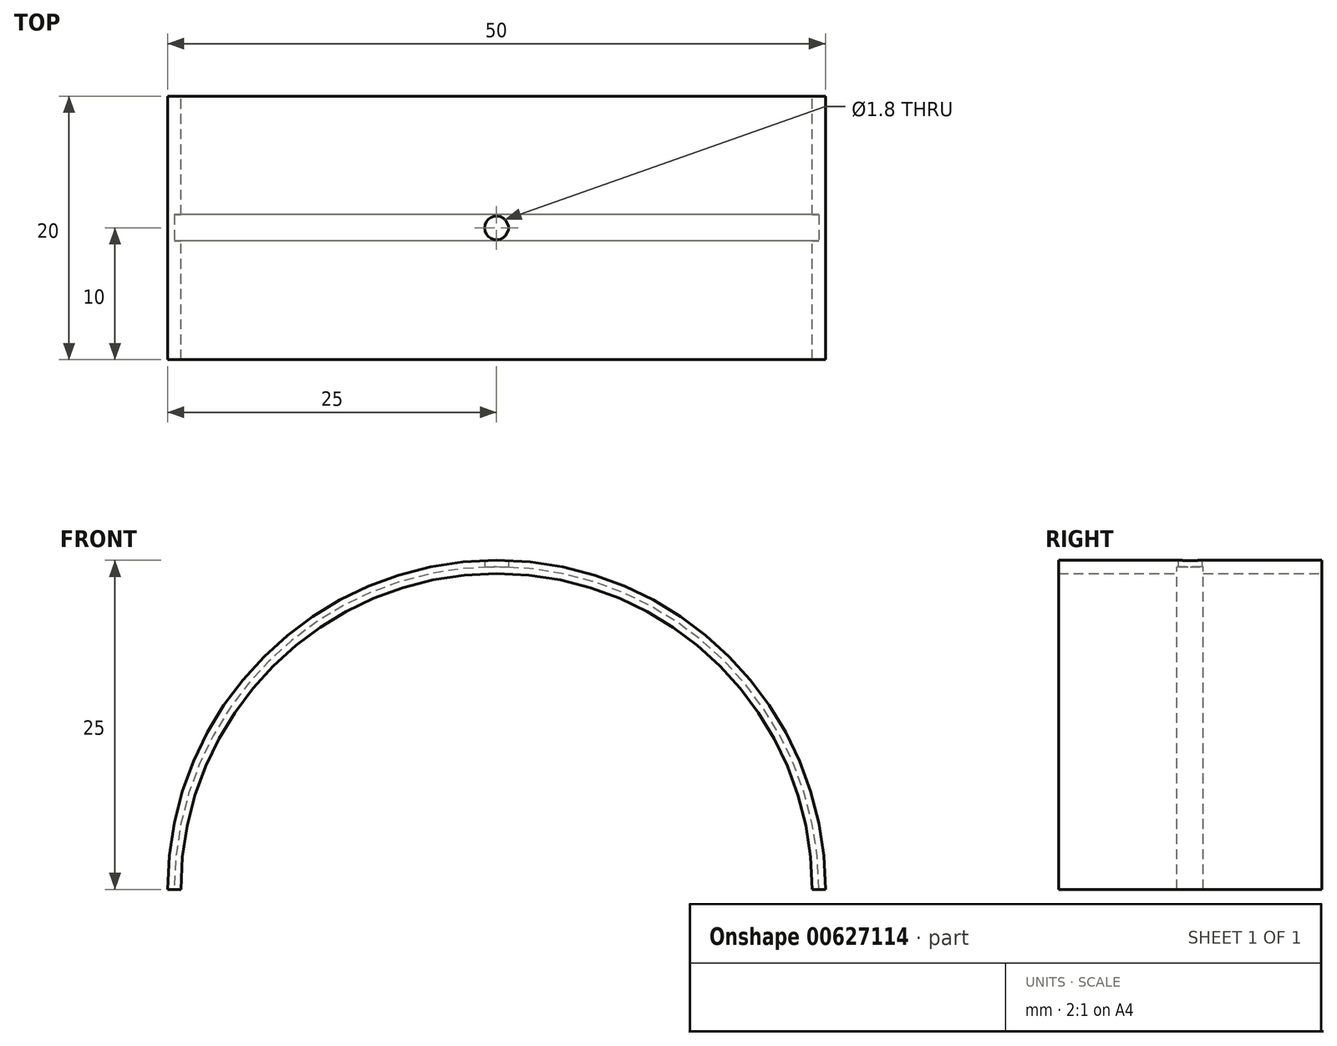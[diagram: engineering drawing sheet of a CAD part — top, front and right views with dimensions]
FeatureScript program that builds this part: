
annotation { "Feature Type Name" : "Feature", "Feature Type Description" : "" }
export const myFeature = defineFeature(function(context is Context, id is Id, definition is map)
    precondition{}
    {
        {
            var Q0;
            Q0=qCreatedBy(makeId("Front.planeOp"),FACE);
            var sketch = newSketch(context, id + "F0", { "sketchPlane" : qUnion([Q0])});
            skArc(sketch, "E0", {"start": v(25, 0) * mm, "mid": v(0, 25) * mm, "end": v(-25, 0) * mm});
            skArc(sketch, "E1.0", {"start": v(24, 0) * mm, "mid": v(0, 24) * mm, "end": v(-24, 0) * mm});
            skLineSegment(sketch, "E2", {"start": v(-25, 0) * mm, "end": v(-24, 0) * mm});
            skLineSegment(sketch, "E3.trimOffspring", {"start": v(24, 0) * mm, "end": v(25, 0) * mm});
            skSolve(sketch);
        }
        {
            var Q0;
            Q0 = qSketchRegion(id + "F0", true);
            extrude(context, id + "F1", {"entities" : qUnion([Q0]), "depth" : 20 * mm, "offsetDistance" : 25 * mm});
        }
        {
            var Q0;
            Q0=makeQuery(id+"F1.opExtrude","SWEPT_FACE",FACE,{"disambiguationData":[OSD([sQuery(id+"F0.wireOp",EDGE,"E2")])]});
            var sketch = newSketch(context, id + "F2", { "sketchPlane" : qUnion([Q0])});
            skLineSegment(sketch, "E4.bottom", {"start": v(-24, 9) * mm, "end": v(-24.5, 9) * mm});
            skLineSegment(sketch, "E4.top", {"start": v(-24, 11) * mm, "end": v(-24.5, 11) * mm});
            skLineSegment(sketch, "E4.left", {"start": v(-24, 9) * mm, "end": v(-24, 11) * mm});
            skLineSegment(sketch, "E4.right", {"start": v(-24.5, 9) * mm, "end": v(-24.5, 11) * mm});
            skPoint(sketch, "E5", {"position": v(-24, 10) * mm});
            skLineSegment(sketch, "E6", {"start": v(0, 0) * mm, "end": v(0, 13.34) * mm, "construction": true});
            skSolve(sketch);
        }
        {
            var Q0;
            Q0 = qSketchRegion(id + "F2", true);
            var Q1;
            Q1=sQuery(id+"F2.wireOp",EDGE,"E6");
            revolve(context, id + "F3", {"operationType" : NewBodyOperationType.REMOVE, "entities" : qUnion([Q0]), "axis" : qUnion([Q1]), "revolveType" : RevolveType.FULL, "oppositeDirection" : true});
        }
        {
            var Q0;
            Q0=makeQuery(id+"F1.opExtrude","SWEPT_FACE",FACE,{"disambiguationData":[OSD([sQuery(id+"F0.wireOp",EDGE,"E2")])]});
            var sketch = newSketch(context, id + "F4", { "sketchPlane" : qUnion([Q0])});
            skCircle(sketch, "E7", {"center": v(0, 10) * mm, "radius": 0.9 * mm});
            skPoint(sketch, "E7.centerSnap0", {"position": v(-24.5, 10) * mm});
            skSolve(sketch);
        }
        {
            var Q0;
            Q0 = qSketchRegion(id + "F4", true);
            extrude(context, id + "F5", {"entities" : qUnion([Q0]), "operationType" : NewBodyOperationType.REMOVE, "endBound" : BoundingType.THROUGH_ALL, "oppositeDirection" : true, "depth" : 25 * mm, "offsetDistance" : 25 * mm});
        }
    });
